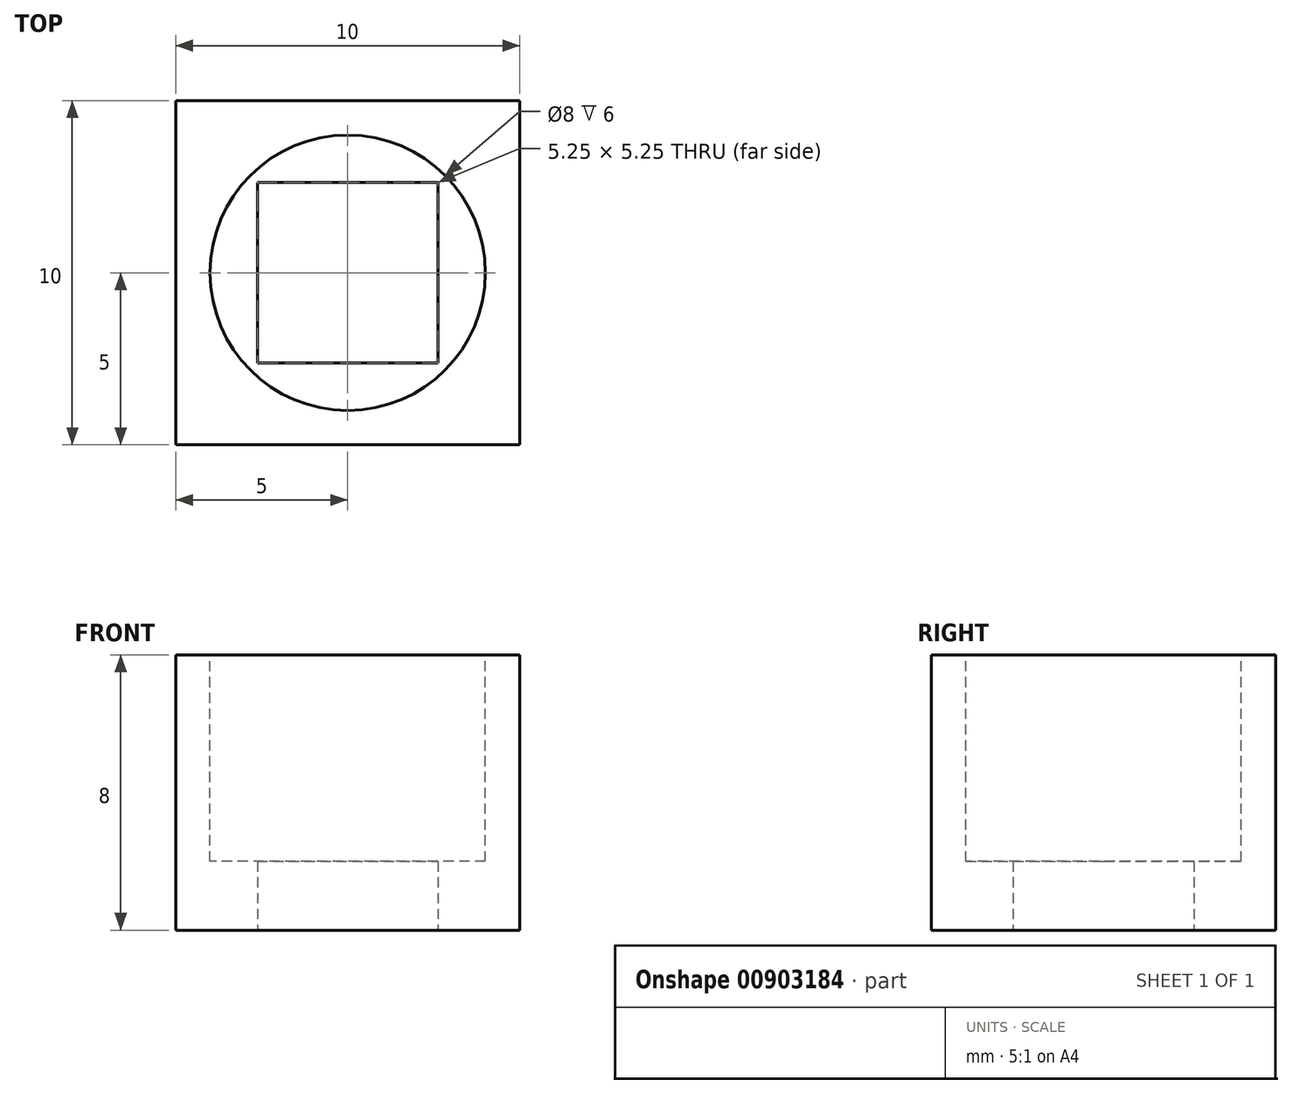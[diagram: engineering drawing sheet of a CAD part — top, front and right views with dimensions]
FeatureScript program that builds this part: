
annotation { "Feature Type Name" : "Feature", "Feature Type Description" : "" }
export const myFeature = defineFeature(function(context is Context, id is Id, definition is map)
    precondition{}
    {
        {
            var Q0;
            Q0=qCreatedBy(makeId("Top.planeOp"),FACE);
            var sketch = newSketch(context, id + "F0", { "sketchPlane" : qUnion([Q0])});
            skCircle(sketch, "E0.cCircle", {"center": v(0, 0) * mm, "radius": 5 * mm, "construction": true});
            skLineSegment(sketch, "E0.0", {"start": v(5, 5) * mm, "end": v(5, -5) * mm});
            skLineSegment(sketch, "E0.1", {"start": v(5, -5) * mm, "end": v(-5, -5) * mm});
            skLineSegment(sketch, "E0.2", {"start": v(-5, -5) * mm, "end": v(-5, 5) * mm});
            skLineSegment(sketch, "E0.3", {"start": v(-5, 5) * mm, "end": v(5, 5) * mm});
            skPoint(sketch, "E0.0.midPoint", {"position": v(5, 0) * mm});
            skSolve(sketch);
        }
        {
            var Q0;
            Q0=makeQuery(id+"F0.imprint","IMPRINT",FACE,{"disambiguationData":[TD([[makeQuery(id+"F0.imprint","IMPRINT",EDGE,{"derivedFrom":sQuery(id+"F0.wireOp",EDGE,"E0.0")}),-1.0]])]});
            var Q1;
            Q1=makeQuery(id+"F0.imprint","IMPRINT",FACE,{"disambiguationData":[TD([[makeQuery(id+"F0.imprint","IMPRINT",EDGE,{"derivedFrom":sQuery(id+"F0.wireOp",EDGE,"bRmwNUet-cvvg-GxDU-oRp2-ykDtNP41wSXA")}),1.0]])]});
            extrude(context, id + "F1", {"entities" : qUnion([Q0, Q1]), "depth" : 8 * mm, "offsetDistance" : 25 * mm});
        }
        {
            var Q0;
            Q0=makeQuery(id+"F1.opExtrude","CAP_FACE",FACE,{"disambiguationData":[OSD([sQuery(id+"F0.wireOp",EDGE,"E0.0"),sQuery(id+"F0.wireOp",EDGE,"E0.1"),sQuery(id+"F0.wireOp",EDGE,"E0.2"),sQuery(id+"F0.wireOp",EDGE,"E0.3")])],"isStart":false});
            var sketch = newSketch(context, id + "F2", { "sketchPlane" : qUnion([Q0])});
            skCircle(sketch, "E1", {"center": v(0, 0) * mm, "radius": 4 * mm});
            skSolve(sketch);
        }
        {
            var Q0;
            Q0=makeQuery(id+"F2.imprint","IMPRINT",FACE,{"disambiguationData":[TD([[makeQuery(id+"F2.imprint","IMPRINT",EDGE,{"derivedFrom":sQuery(id+"F2.wireOp",EDGE,"E1")}),1.0]])]});
            extrude(context, id + "F3", {"entities" : qUnion([Q0]), "operationType" : NewBodyOperationType.REMOVE, "oppositeDirection" : true, "depth" : 6 * mm, "offsetDistance" : 25 * mm});
        }
        {
            var Q0;
            Q0=makeQuery(id+"F0.imprint","IMPRINT",FACE,{"disambiguationData":[TD([[makeQuery(id+"F0.imprint","IMPRINT",EDGE,{"derivedFrom":sQuery(id+"F0.wireOp",EDGE,"E0.0")}),-1.0]])]});
            var sketch = newSketch(context, id + "F4", { "sketchPlane" : qUnion([Q0])});
            skLineSegment(sketch, "E2.bottom", {"start": v(2.62, -2.62) * mm, "end": v(-2.62, -2.63) * mm});
            skLineSegment(sketch, "E2.top", {"start": v(2.62, 2.63) * mm, "end": v(-2.62, 2.62) * mm});
            skLineSegment(sketch, "E2.left", {"start": v(2.62, -2.62) * mm, "end": v(2.62, 2.63) * mm});
            skLineSegment(sketch, "E2.right", {"start": v(-2.62, -2.63) * mm, "end": v(-2.62, 2.62) * mm});
            skPoint(sketch, "E2.middle", {"position": v(0, 0) * mm});
            skSolve(sketch);
        }
        {
            var Q0;
            Q0 = qSketchRegion(id + "F4", true);
            extrude(context, id + "F5", {"entities" : qUnion([Q0]), "operationType" : NewBodyOperationType.REMOVE, "depth" : 3 * mm, "offsetDistance" : 25 * mm});
        }
    });
